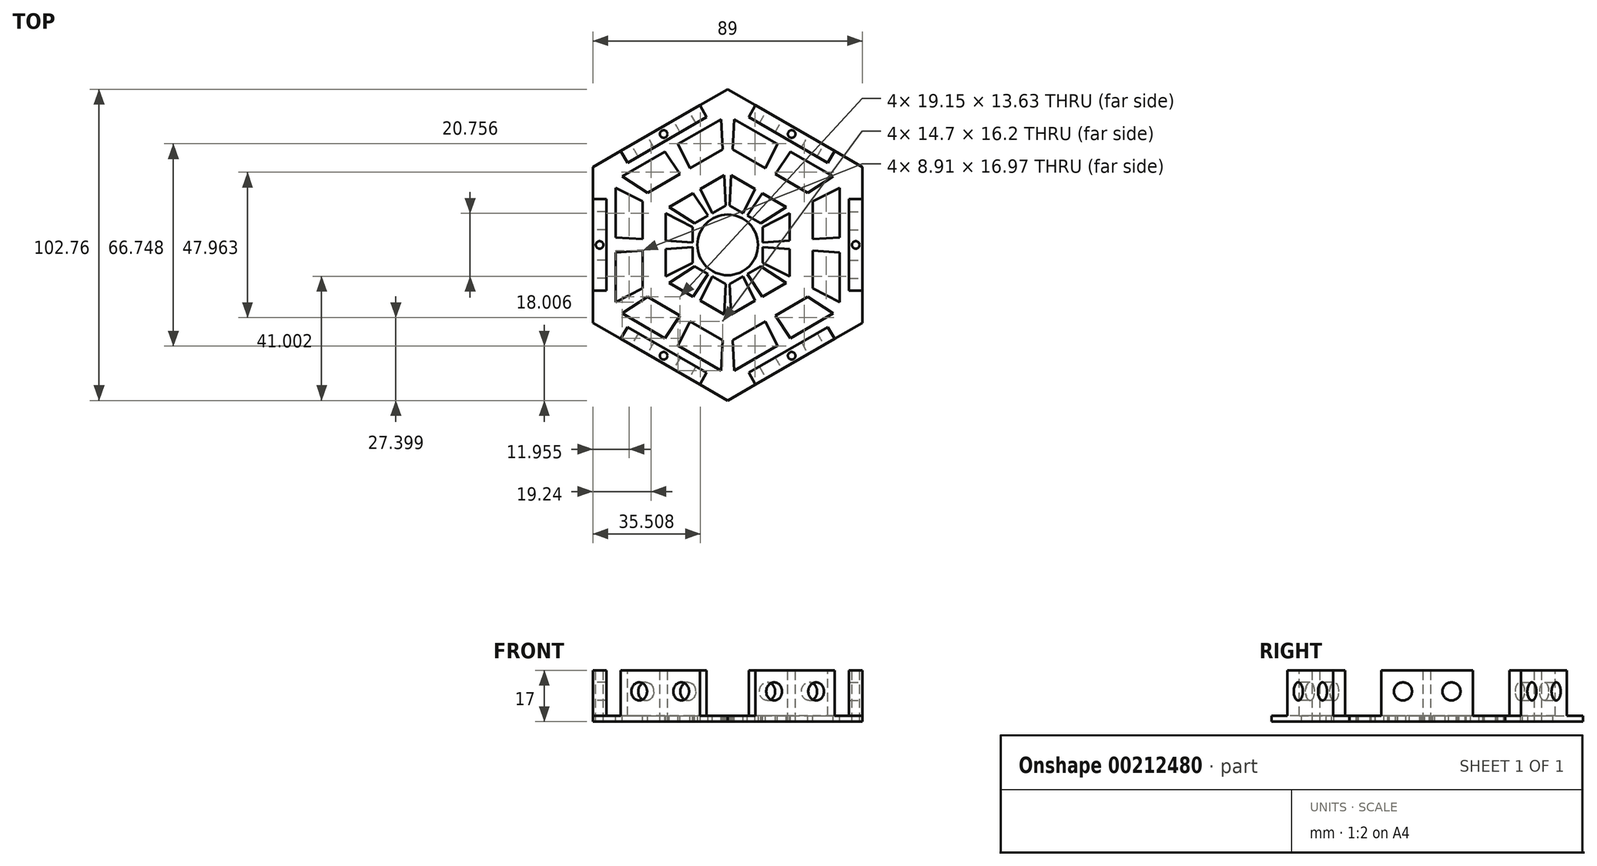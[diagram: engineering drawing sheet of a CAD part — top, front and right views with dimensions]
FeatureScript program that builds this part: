
annotation { "Feature Type Name" : "Feature", "Feature Type Description" : "" }
export const myFeature = defineFeature(function(context is Context, id is Id, definition is map)
    precondition{}
    {
        {
            var Q0;
            Q0=qCreatedBy(makeId("Top.planeOp"),FACE);
            var sketch = newSketch(context, id + "F0", { "sketchPlane" : qUnion([Q0])});
            skCircle(sketch, "E0.cCircle", {"center": v(0, 0) * mm, "radius": 40 * mm, "construction": true});
            skLineSegment(sketch, "E0.0", {"start": v(40, 23.1) * mm, "end": v(40, -23.1) * mm, "construction": true});
            skLineSegment(sketch, "E0.1", {"start": v(40, -23.1) * mm, "end": v(0, -46.19) * mm, "construction": true});
            skLineSegment(sketch, "E0.2", {"start": v(0, -46.19) * mm, "end": v(-40, -23.1) * mm, "construction": true});
            skLineSegment(sketch, "E0.3", {"start": v(-40, -23.1) * mm, "end": v(-40, 23.1) * mm, "construction": true});
            skLineSegment(sketch, "E0.4", {"start": v(-40, 23.1) * mm, "end": v(0, 46.19) * mm, "construction": true});
            skLineSegment(sketch, "E0.5", {"start": v(0, 46.19) * mm, "end": v(40, 23.1) * mm, "construction": true});
            skPoint(sketch, "E0.0.midPoint", {"position": v(40, 0) * mm});
            skLineSegment(sketch, "E1.0", {"start": v(-44.5, -25.7) * mm, "end": v(-44.5, 25.7) * mm});
            skLineSegment(sketch, "E1.1", {"start": v(0, 51.38) * mm, "end": v(44.5, 25.7) * mm});
            skLineSegment(sketch, "E1.2", {"start": v(44.5, 25.7) * mm, "end": v(44.5, -25.7) * mm});
            skLineSegment(sketch, "E1.3", {"start": v(-44.5, 25.7) * mm, "end": v(0, 51.38) * mm});
            skLineSegment(sketch, "E1.4", {"start": v(44.5, -25.7) * mm, "end": v(0, -51.38) * mm});
            skLineSegment(sketch, "E1.5", {"start": v(0, -51.38) * mm, "end": v(-44.5, -25.7) * mm});
            skCircle(sketch, "E2", {"center": v(0, 0) * mm, "radius": 10 * mm});
            skSolve(sketch);
        }
        {
            var Q0;
            Q0 = qSketchRegion(id + "F0", true);
            var Q1;
            Q1=sQuery(id+"F0.wireOp",EDGE,"E1.3");
            var Q2;
            Q2=sQuery(id+"F0.wireOp",EDGE,"E1.1");
            var Q3;
            Q3=sQuery(id+"F0.wireOp",EDGE,"E1.2");
            var Q4;
            Q4=sQuery(id+"F0.wireOp",EDGE,"E1.4");
            var Q5;
            Q5=sQuery(id+"F0.wireOp",EDGE,"E1.5");
            var Q6;
            Q6=sQuery(id+"F0.wireOp",EDGE,"E1.0");
            var Q7;
            Q7=sQuery(id+"F0.wireOp",EDGE,"E2");
            extrude(context, id + "F1", {"entities" : qUnion([Q0]), "surfaceEntities" : qUnion([Q1, Q2, Q3, Q4, Q5, Q6, Q7]), "depth" : 2 * mm});
        }
        {
            var Q0;
            Q0=makeQuery(id+"F1.opExtrude","CAP_FACE",FACE,{"disambiguationData":[OSD([sQuery(id+"F0.wireOp",EDGE,"E1.0"),sQuery(id+"F0.wireOp",EDGE,"E1.1"),sQuery(id+"F0.wireOp",EDGE,"E1.2"),sQuery(id+"F0.wireOp",EDGE,"E1.3"),sQuery(id+"F0.wireOp",EDGE,"E1.4"),sQuery(id+"F0.wireOp",EDGE,"E1.5"),sQuery(id+"F0.wireOp",EDGE,"E2")])],"isStart":false});
            var sketch = newSketch(context, id + "F2", { "sketchPlane" : qUnion([Q0])});
            skCircle(sketch, "E3.cCircle", {"center": v(0, 0) * mm, "radius": 44.5 * mm, "construction": true});
            skLineSegment(sketch, "E3.0", {"start": v(0, 51.38) * mm, "end": v(44.5, 25.7) * mm});
            skLineSegment(sketch, "E3.1", {"start": v(44.5, 25.7) * mm, "end": v(44.5, -25.7) * mm});
            skLineSegment(sketch, "E3.2", {"start": v(44.5, -25.7) * mm, "end": v(0, -51.38) * mm});
            skLineSegment(sketch, "E3.3", {"start": v(0, -51.38) * mm, "end": v(-44.5, -25.7) * mm});
            skLineSegment(sketch, "E3.4", {"start": v(-44.5, -25.7) * mm, "end": v(-44.5, 25.7) * mm});
            skLineSegment(sketch, "E3.5", {"start": v(-44.5, 25.7) * mm, "end": v(0, 51.38) * mm});
            skPoint(sketch, "E3.0.midPoint", {"position": v(22.25, 38.54) * mm});
            skLineSegment(sketch, "E4.0", {"start": v(-40, -23.1) * mm, "end": v(-40, 23.1) * mm});
            skLineSegment(sketch, "E4.1", {"start": v(0, 46.19) * mm, "end": v(40, 23.1) * mm});
            skLineSegment(sketch, "E4.2", {"start": v(40, 23.1) * mm, "end": v(40, -23.1) * mm});
            skLineSegment(sketch, "E4.3", {"start": v(-40, 23.1) * mm, "end": v(0, 46.19) * mm});
            skLineSegment(sketch, "E4.4", {"start": v(40, -23.1) * mm, "end": v(0, -46.19) * mm});
            skLineSegment(sketch, "E4.5", {"start": v(0, -46.19) * mm, "end": v(-40, -23.1) * mm});
            skSolve(sketch);
        }
        {
            var Q0;
            Q0 = qSketchRegion(id + "F2", true);
            extrude(context, id + "F3", {"entities" : qUnion([Q0]), "operationType" : NewBodyOperationType.ADD, "depth" : 15 * mm});
        }
        {
            var Q0;
            Q0=makeQuery(id+"F3.opExtrude","CAP_FACE",FACE,{"disambiguationData":[OSD([sQuery(id+"F2.wireOp",EDGE,"E3.0"),sQuery(id+"F2.wireOp",EDGE,"E3.1"),sQuery(id+"F2.wireOp",EDGE,"E3.2"),sQuery(id+"F2.wireOp",EDGE,"E3.3"),sQuery(id+"F2.wireOp",EDGE,"E3.4"),sQuery(id+"F2.wireOp",EDGE,"E3.5"),sQuery(id+"F2.wireOp",EDGE,"E4.0"),sQuery(id+"F2.wireOp",EDGE,"E4.1"),sQuery(id+"F2.wireOp",EDGE,"E4.2"),sQuery(id+"F2.wireOp",EDGE,"E4.3"),sQuery(id+"F2.wireOp",EDGE,"E4.4"),sQuery(id+"F2.wireOp",EDGE,"E4.5")])],"isStart":false});
            var sketch = newSketch(context, id + "F4", { "sketchPlane" : qUnion([Q0])});
            skCircle(sketch, "E5", {"center": v(-21.13, 36.59) * mm, "radius": 1.25 * mm});
            skLineSegment(sketch, "E6", {"start": v(-22.25, 38.54) * mm, "end": v(-20, 34.64) * mm, "construction": true});
            skCircle(sketch, "E7.1.0", {"center": v(-42.25, 0) * mm, "radius": 1.25 * mm});
            skCircle(sketch, "E7.2.0", {"center": v(-21.13, -36.59) * mm, "radius": 1.25 * mm});
            skCircle(sketch, "E7.3.0", {"center": v(21.13, -36.59) * mm, "radius": 1.25 * mm});
            skCircle(sketch, "E7.4.0", {"center": v(42.25, 0) * mm, "radius": 1.25 * mm});
            skCircle(sketch, "E7.5.0", {"center": v(21.13, 36.59) * mm, "radius": 1.25 * mm});
            skPoint(sketch, "E7.center", {"position": v(0, 0) * mm});
            skSolve(sketch);
        }
        {
            var Q0;
            Q0 = qSketchRegion(id + "F4", true);
            extrude(context, id + "F5", {"entities" : qUnion([Q0]), "operationType" : NewBodyOperationType.REMOVE, "endBound" : BoundingType.THROUGH_ALL, "oppositeDirection" : true, "depth" : 25 * mm});
        }
        {
            var Q0;
            Q0=makeQuery(id+"F3.boolean.opBoolean","MERGE",FACE,{"derivedFrom":[makeQuery(id+"F1.opExtrude","SWEPT_FACE",FACE,{"disambiguationData":[OSD([sQuery(id+"F0.wireOp",EDGE,"E1.5")])]}),makeQuery(id+"F3.opExtrude","SWEPT_FACE",FACE,{"disambiguationData":[OSD([sQuery(id+"F2.wireOp",EDGE,"E3.3")])]})]});
            var sketch = newSketch(context, id + "F6", { "sketchPlane" : qUnion([Q0])});
            skLineSegment(sketch, "E8", {"start": v(-8, 10) * mm, "end": v(8, 10) * mm, "construction": true});
            skLineSegment(sketch, "E9", {"start": v(-8, 10) * mm, "end": v(-25.7, 10) * mm, "construction": true});
            skLineSegment(sketch, "E10", {"start": v(8, 10) * mm, "end": v(25.7, 10) * mm, "construction": true});
            skCircle(sketch, "E11", {"center": v(-8, 10) * mm, "radius": 3 * mm});
            skCircle(sketch, "E12", {"center": v(8, 10) * mm, "radius": 3 * mm});
            skSolve(sketch);
        }
        {
            var Q0;
            Q0 = qSketchRegion(id + "F6", true);
            extrude(context, id + "F7", {"entities" : qUnion([Q0]), "endBound" : BoundingType.UP_TO_NEXT, "oppositeDirection" : true, "depth" : 25 * mm});
        }
        {
            var Q0;
            Q0=makeQuery(id+"F3.opExtrude","CAP_FACE",FACE,{"disambiguationData":[OSD([sQuery(id+"F2.wireOp",EDGE,"E3.0"),sQuery(id+"F2.wireOp",EDGE,"E3.1"),sQuery(id+"F2.wireOp",EDGE,"E3.2"),sQuery(id+"F2.wireOp",EDGE,"E3.3"),sQuery(id+"F2.wireOp",EDGE,"E3.4"),sQuery(id+"F2.wireOp",EDGE,"E3.5"),sQuery(id+"F2.wireOp",EDGE,"E4.0"),sQuery(id+"F2.wireOp",EDGE,"E4.1"),sQuery(id+"F2.wireOp",EDGE,"E4.2"),sQuery(id+"F2.wireOp",EDGE,"E4.3"),sQuery(id+"F2.wireOp",EDGE,"E4.4"),sQuery(id+"F2.wireOp",EDGE,"E4.5")])],"isStart":false});
            var sketch = newSketch(context, id + "F8", { "sketchPlane" : qUnion([Q0])});
            skLineSegment(sketch, "E13", {"start": v(-44.5, -25.7) * mm, "end": v(-40, -23.1) * mm});
            skLineSegment(sketch, "E14", {"start": v(0, -46.19) * mm, "end": v(0, -51.38) * mm});
            skLineSegment(sketch, "E15", {"start": v(-40, -23.1) * mm, "end": v(-33.07, -27.1) * mm});
            skLineSegment(sketch, "E16", {"start": v(-33.07, -27.1) * mm, "end": v(-6.93, -42.19) * mm, "construction": true});
            skLineSegment(sketch, "E17", {"start": v(-6.93, -42.19) * mm, "end": v(0, -46.19) * mm});
            skLineSegment(sketch, "E18", {"start": v(0, -51.38) * mm, "end": v(-9.18, -46.09) * mm});
            skLineSegment(sketch, "E19", {"start": v(-9.18, -46.09) * mm, "end": v(-35.32, -31) * mm, "construction": true});
            skLineSegment(sketch, "E20", {"start": v(-35.32, -31) * mm, "end": v(-44.5, -25.7) * mm});
            skLineSegment(sketch, "E21", {"start": v(-33.07, -27.1) * mm, "end": v(-35.32, -31) * mm});
            skLineSegment(sketch, "E22", {"start": v(-9.18, -46.09) * mm, "end": v(-6.93, -42.19) * mm});
            skSolve(sketch);
        }
        {
            var Q0;
            Q0 = qSketchRegion(id + "F8", true);
            var Q1;
            Q1=makeQuery(id+"F1.opExtrude","CAP_FACE",FACE,{"disambiguationData":[OSD([sQuery(id+"F0.wireOp",EDGE,"E1.0"),sQuery(id+"F0.wireOp",EDGE,"E1.1"),sQuery(id+"F0.wireOp",EDGE,"E1.2"),sQuery(id+"F0.wireOp",EDGE,"E1.3"),sQuery(id+"F0.wireOp",EDGE,"E1.4"),sQuery(id+"F0.wireOp",EDGE,"E1.5"),sQuery(id+"F0.wireOp",EDGE,"E2")])],"isStart":false});
            extrude(context, id + "F9", {"entities" : qUnion([Q0]), "endBound" : BoundingType.UP_TO_SURFACE, "oppositeDirection" : true, "endBoundEntityFace" : qUnion([Q1]), "depth" : 25 * mm});
        }
        {
            var Q0;
            {var subQ0=sQuery(id+"F0.wireOp",EDGE,"E2");var subQ1=sQuery(id+"F0.wireOp",EDGE,"E1.5");var subQ2=sQuery(id+"F0.wireOp",EDGE,"E1.4");var subQ3=sQuery(id+"F0.wireOp",EDGE,"E1.3");var subQ4=sQuery(id+"F0.wireOp",EDGE,"E1.2");var subQ5=sQuery(id+"F0.wireOp",EDGE,"E1.1");var subQ6=sQuery(id+"F0.wireOp",EDGE,"E1.0");var subQ7=makeQuery(id+"F9.opExtrude","CAP_FACE",FACE,{"disambiguationData":[OSD([subQ6,subQ5,subQ4,subQ3,subQ2,subQ1,subQ0]),ownerDisambiguation([makeQuery(id+"F9.opExtrude","SWEPT_BODY",BODY,{"disambiguationData":[OSD([sQuery(id+"F8.wireOp",EDGE,"E14"),sQuery(id+"F8.wireOp",EDGE,"E17"),sQuery(id+"F8.wireOp",EDGE,"E18"),sQuery(id+"F8.wireOp",EDGE,"E22")])]})])],"isStart":false});var subQ8=makeQuery(id+"F9.opExtrude","CAP_FACE",FACE,{"disambiguationData":[OSD([subQ6,subQ5,subQ4,subQ3,subQ2,subQ1,subQ0]),ownerDisambiguation([makeQuery(id+"F9.opExtrude","SWEPT_BODY",BODY,{"disambiguationData":[OSD([sQuery(id+"F8.wireOp",EDGE,"E13"),sQuery(id+"F8.wireOp",EDGE,"E15"),sQuery(id+"F8.wireOp",EDGE,"E20"),sQuery(id+"F8.wireOp",EDGE,"E21")])]})])],"isStart":false});Q0=makeQuery(id+"F12.boolean.opBoolean","MERGE",FACE,{"derivedFrom":[makeQuery(id+"F1.opExtrude","CAP_FACE",FACE,{"disambiguationData":[OSD([subQ6,subQ5,subQ4,subQ3,subQ2,subQ1,subQ0])],"isStart":false}),subQ8,subQ7,makeQuery(id+"F12.opPattern","COPY",FACE,{"derivedFrom":subQ8,"instanceName":"1"}),makeQuery(id+"F12.opPattern","COPY",FACE,{"derivedFrom":subQ7,"instanceName":"1"}),makeQuery(id+"F12.opPattern","COPY",FACE,{"derivedFrom":subQ8,"instanceName":"2"}),makeQuery(id+"F12.opPattern","COPY",FACE,{"derivedFrom":subQ7,"instanceName":"2"}),makeQuery(id+"F12.opPattern","COPY",FACE,{"derivedFrom":subQ8,"instanceName":"3"}),makeQuery(id+"F12.opPattern","COPY",FACE,{"derivedFrom":subQ7,"instanceName":"3"}),makeQuery(id+"F12.opPattern","COPY",FACE,{"derivedFrom":subQ8,"instanceName":"4"}),makeQuery(id+"F12.opPattern","COPY",FACE,{"derivedFrom":subQ7,"instanceName":"4"}),makeQuery(id+"F12.opPattern","COPY",FACE,{"derivedFrom":subQ8,"instanceName":"5"}),makeQuery(id+"F12.opPattern","COPY",FACE,{"derivedFrom":subQ7,"instanceName":"5"})]});}
            var sketch = newSketch(context, id + "F10", { "sketchPlane" : qUnion([Q0])});
            skLineSegment(sketch, "E23", {"start": v(-16.34, -33.3) * mm, "end": v(-2.17, -41.47) * mm});
            skLineSegment(sketch, "E24", {"start": v(-16.34, -33.3) * mm, "end": v(-12.4, -25.27) * mm});
            skLineSegment(sketch, "E25", {"start": v(-1.64, -31.49) * mm, "end": v(-12.4, -25.27) * mm});
            skLineSegment(sketch, "E26", {"start": v(-1.64, -31.49) * mm, "end": v(-2.17, -41.47) * mm});
            skLineSegment(sketch, "E27", {"start": v(-5.11, -10.42) * mm, "end": v(-0.68, -12.98) * mm});
            skLineSegment(sketch, "E28", {"start": v(-5.11, -10.42) * mm, "end": v(-9.05, -18.44) * mm});
            skLineSegment(sketch, "E29", {"start": v(-1.2, -22.97) * mm, "end": v(-9.05, -18.44) * mm});
            skLineSegment(sketch, "E30", {"start": v(-1.2, -22.97) * mm, "end": v(-0.68, -12.98) * mm});
            skLineSegment(sketch, "E31", {"start": v(0, 0) * mm, "end": v(-5.11, -10.42) * mm, "construction": true});
            skLineSegment(sketch, "E32", {"start": v(-0.68, -12.98) * mm, "end": v(0, 0) * mm, "construction": true});
            skLineSegment(sketch, "E33", {"start": v(-1.2, -22.97) * mm, "end": v(-1.64, -31.49) * mm, "construction": true});
            skLineSegment(sketch, "E34", {"start": v(-9.05, -18.44) * mm, "end": v(-12.4, -25.27) * mm, "construction": true});
            skLineSegment(sketch, "E35", {"start": v(0, 0) * mm, "end": v(0, -46.19) * mm, "construction": true});
            skLineSegment(sketch, "E36", {"start": v(0, 0) * mm, "end": v(-20, -34.64) * mm, "construction": true});
            skLineSegment(sketch, "E37", {"start": v(-2.17, -41.47) * mm, "end": v(0, -42.72) * mm, "construction": true});
            skLineSegment(sketch, "E38", {"start": v(-16.34, -33.3) * mm, "end": v(-18.58, -32.19) * mm, "construction": true});
            skLineSegment(sketch, "E39.MirrorCS", {"start": v(-6.47, -9.64) * mm, "end": v(-11.44, -17.06) * mm});
            skLineSegment(sketch, "E40.MirrorCS", {"start": v(-6.47, -9.64) * mm, "end": v(-10.9, -7.08) * mm});
            skLineSegment(sketch, "E41.MirrorCS", {"start": v(-19.3, -12.52) * mm, "end": v(-10.9, -7.08) * mm});
            skLineSegment(sketch, "E42.MirrorCS", {"start": v(-19.3, -12.52) * mm, "end": v(-11.44, -17.06) * mm});
            skLineSegment(sketch, "E43.MirrorCS", {"start": v(-26.45, -17.17) * mm, "end": v(-15.69, -23.38) * mm});
            skLineSegment(sketch, "E44.MirrorCS", {"start": v(-20.66, -30.8) * mm, "end": v(-15.69, -23.38) * mm});
            skLineSegment(sketch, "E45.MirrorCS", {"start": v(-20.66, -30.8) * mm, "end": v(-34.83, -22.61) * mm});
            skLineSegment(sketch, "E46.MirrorCS", {"start": v(-26.45, -17.17) * mm, "end": v(-34.83, -22.61) * mm});
            skSolve(sketch);
        }
        {
            var Q0;
            Q0 = qSketchRegion(id + "F10", true);
            var Q1;
            Q1=makeQuery(id+"F1.opExtrude","CAP_FACE",FACE,{"disambiguationData":[OSD([sQuery(id+"F0.wireOp",EDGE,"E1.0"),sQuery(id+"F0.wireOp",EDGE,"E1.1"),sQuery(id+"F0.wireOp",EDGE,"E1.2"),sQuery(id+"F0.wireOp",EDGE,"E1.3"),sQuery(id+"F0.wireOp",EDGE,"E1.4"),sQuery(id+"F0.wireOp",EDGE,"E1.5"),sQuery(id+"F0.wireOp",EDGE,"E2")])],"isStart":true});
            extrude(context, id + "F11", {"entities" : qUnion([Q0]), "endBound" : BoundingType.UP_TO_SURFACE, "oppositeDirection" : true, "endBoundEntityFace" : qUnion([Q1]), "depth" : 25 * mm});
        }
        {
            var Q0;
            Q0=makeQuery(id+"F7.opExtrude","SWEPT_BODY",BODY,{"disambiguationData":[OSD([sQuery(id+"F6.wireOp",EDGE,"E11")])]});
            var Q1;
            Q1=makeQuery(id+"F7.opExtrude","SWEPT_BODY",BODY,{"disambiguationData":[OSD([sQuery(id+"F6.wireOp",EDGE,"E12")])]});
            var Q2;
            Q2=makeQuery(id+"F9.opExtrude","SWEPT_BODY",BODY,{"disambiguationData":[OSD([sQuery(id+"F8.wireOp",EDGE,"E13"),sQuery(id+"F8.wireOp",EDGE,"E15"),sQuery(id+"F8.wireOp",EDGE,"E20"),sQuery(id+"F8.wireOp",EDGE,"E21")])]});
            var Q3;
            Q3=makeQuery(id+"F9.opExtrude","SWEPT_BODY",BODY,{"disambiguationData":[OSD([sQuery(id+"F8.wireOp",EDGE,"E14"),sQuery(id+"F8.wireOp",EDGE,"E17"),sQuery(id+"F8.wireOp",EDGE,"E18"),sQuery(id+"F8.wireOp",EDGE,"E22")])]});
            var Q4;
            Q4=makeQuery(id+"F11.opExtrude","SWEPT_BODY",BODY,{"disambiguationData":[OSD([sQuery(id+"F10.wireOp",EDGE,"E43.MirrorCS"),sQuery(id+"F10.wireOp",EDGE,"E44.MirrorCS"),sQuery(id+"F10.wireOp",EDGE,"E45.MirrorCS"),sQuery(id+"F10.wireOp",EDGE,"E46.MirrorCS")])]});
            var Q5;
            Q5=makeQuery(id+"F11.opExtrude","SWEPT_BODY",BODY,{"disambiguationData":[OSD([sQuery(id+"F10.wireOp",EDGE,"E39.MirrorCS"),sQuery(id+"F10.wireOp",EDGE,"E40.MirrorCS"),sQuery(id+"F10.wireOp",EDGE,"E41.MirrorCS"),sQuery(id+"F10.wireOp",EDGE,"E42.MirrorCS")])]});
            var Q6;
            Q6=makeQuery(id+"F11.opExtrude","SWEPT_BODY",BODY,{"disambiguationData":[OSD([sQuery(id+"F10.wireOp",EDGE,"E27"),sQuery(id+"F10.wireOp",EDGE,"E28"),sQuery(id+"F10.wireOp",EDGE,"E29"),sQuery(id+"F10.wireOp",EDGE,"E30")])]});
            var Q7;
            Q7=makeQuery(id+"F11.opExtrude","SWEPT_BODY",BODY,{"disambiguationData":[OSD([sQuery(id+"F10.wireOp",EDGE,"E23"),sQuery(id+"F10.wireOp",EDGE,"E24"),sQuery(id+"F10.wireOp",EDGE,"E25"),sQuery(id+"F10.wireOp",EDGE,"E26")])]});
            var Q8;
            Q8=makeQuery(id+"F1.opExtrude","CAP_EDGE",EDGE,{"disambiguationData":[OSD([sQuery(id+"F0.wireOp",EDGE,"E2")])],"isStart":false});
            circularPattern(context, id + "F12", {"operationType" : NewBodyOperationType.REMOVE, "entities" : qUnion([Q0, Q1, Q2, Q3, Q4, Q5, Q6, Q7]), "axis" : qUnion([Q8]), "angle" : 360 * degree, "instanceCount" : 6, "equalSpace" : true});
        }
    });
